# Revit family: Geberit Selnova Square countertop washbasin_PRO_335172
name_source: partatom
category: Plumbing Fixtures
revit_build: Autodesk Revit 2018 (Build: 20190510_1515(x64)
units: mm (PartAtom-declared; Revit-internal decimal feet)

## family parameters
Always vertical = Yes
Cut with Voids When Loaded = No
OmniClass Number = 23.45.05.21
OmniClass Title = Plumbing Fixtures - Sanitary Disposal Units
Part Type = Normal
Room Calculation Point = Yes
Round Connector Dimension = Use Diameter
Shared = No
Work Plane-Based = No

## types (2) — shared parameters
Application purposes = For mounting in washtops from above
Application range = Plumbing fixture
BIM Content Version = GEB MG 1.2
BIM Content revision date = 2020.05.18
Brand = Geberit
CW Connection = Yes
Colour / surface = white
Description = Geberit Selnova Square countertop washbasin
GEB_culture = en-EU
GEB_generic_description = Bathroom collection
GEB_generic_manufacturer = generic
GEB_pimversion = 22.02.10
GEB_processing_type = T
GEB_reference = PRO_335172
GEB_translations = {"ATT_10673":"EAN code basic data","ATT_10882":"Product material","ATT_459792":"Colour / surface","applicationPurposes":"Application purposes","application_range":"Application range","brandName":"Brand","characteristics":"Characteristics","content_creator":"BIM Content creator","content_date_changed":"BIM Content revision date","content_version":"BIM Content Version","key 1000":"Article number key","name":"Name","productBrand":"Product brand","scopeOfDelivery":"Scope of delivery","type":"Type","fixed_material":"Main material"}
HW Connection = No
IfcDescription = Geberit Selnova Square countertop washbasin
IfcExportAs = IfcSanitaryTerminal
IfcExportType = WASHHANDBASIN
LOD300 = No
LOD400 = Yes
Main material = Geberit, Plastic, Opaque white
Manufacturer = Geberit
Name = Geberit Selnova Square countertop washbasin
Product material = Vitreous china
Scope of delivery = Fastening material
Vent Connection = No
Waste Connection = Yes
outlet_flow = 0.0 L/s

## per-type parameters (varying)
| type | 500306_0_view | 500307_0_view | Article number key | EAN code basic data |
| 500.306.01.1 Geberit Selnova Square countertop washbasin | Yes | No | 500.306.01.1 | 4025416530022 |
| 500.307.01.1 Geberit Selnova Square countertop washbasin | No | Yes | 500.307.01.1 | 4025416530046 |

## geometry (parser evidence)
native form markers: Blend x8, Sweep x18
no freeform markers — native parametric forms only
